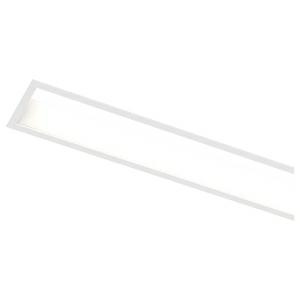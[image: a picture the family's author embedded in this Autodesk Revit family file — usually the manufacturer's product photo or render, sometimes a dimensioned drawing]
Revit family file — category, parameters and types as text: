
# Revit family: groove_l_2020_eb_led_37w_2386lm_3000k_cri80_230-2110_c45c
name_source: partatom
category: Leuchten
revit_build: Autodesk Revit 2016 (Build: 20190508_0715(x64)
units: mm (PartAtom-declared; Revit-internal decimal feet)

## family parameters
Basisbauteil = Fläche
Beim Laden mit Abzugskörper schneiden = Nein
Bemaßung runder Anschluss = Durchmesser verwenden
Gemeinsam genutzt = Nein
Lichtquelle = Nein
Raumberechnungspunkt = Nein
Teiletyp = Normal

## types (1)
- 230-2110- (7 x LED, 710 lm, 5.1 W, 3000K)
    Beschreibung = The recessed luminaire GROOVE from the familiy GROOVE consists of aluminum-extruded profile. Charming SOFT-EDGE design ensure unparalleled styling. The ballast is integrated and allows for an operation with 220-240V (50.60Hz). GROOVE (# 230-2110) ist not dimmable (on/off). The luminaire with direct illumination and corresponds to protection class SK1 at IP20.
    CIE Flux Codes = 59 87 97 100 49
    Color Rendering = 1B/80…89
    Color Temperature = 3000K
    Height = 0 mm  [stored 0 ft]
    Hersteller = Prolicht
    Lamp Light Flux = 710 lm
    Lamp Power = 5.1 W
    Lamp count = 7
    Lampe = 7 x LED
    Length = 2020 mm
    Luminous efficacy = 67 lm/W
    ModVariant = Nein
    Modell = 230-2110
    Mounting Place = Ceiling
    Mounting Type = Recessed
    Number of Poles = 1
    OnlyDefault = Ja
    Power Factor = 1
    Product Name = GROOVE L=2020 EB LED 37W 2386lm 3000K CRI80
    Product group = Recessed profile lights
    ProductGroupID = 423
    Protection Class = Protection class
    Protection Degree = Degree of protection
    RLX_Detail_Level = 1
    RlxData = <blob elided: 171397 chars, md5=39c70aef>
    Scheinlast = 36 VA
    Socket = socket
    Standby Power = 0 W
    System Light Flux = 2397 lm
    System Power = 36 W
    Typenbild = 230-2110.jpg
    URL = http://relux.com
    VarID = 230-2110-
    Voltage = 0 V
    Vorgabe-Ansicht = 1800 mm
    Weight = 0.00 kg
    Width = 92 mm

note: [stored X ft] marks values corroborated as IEEE doubles in the binary element streams (Revit-internal decimal feet)

## geometry (parser evidence)
native form markers: Sweep x7
no freeform markers — native parametric forms only
